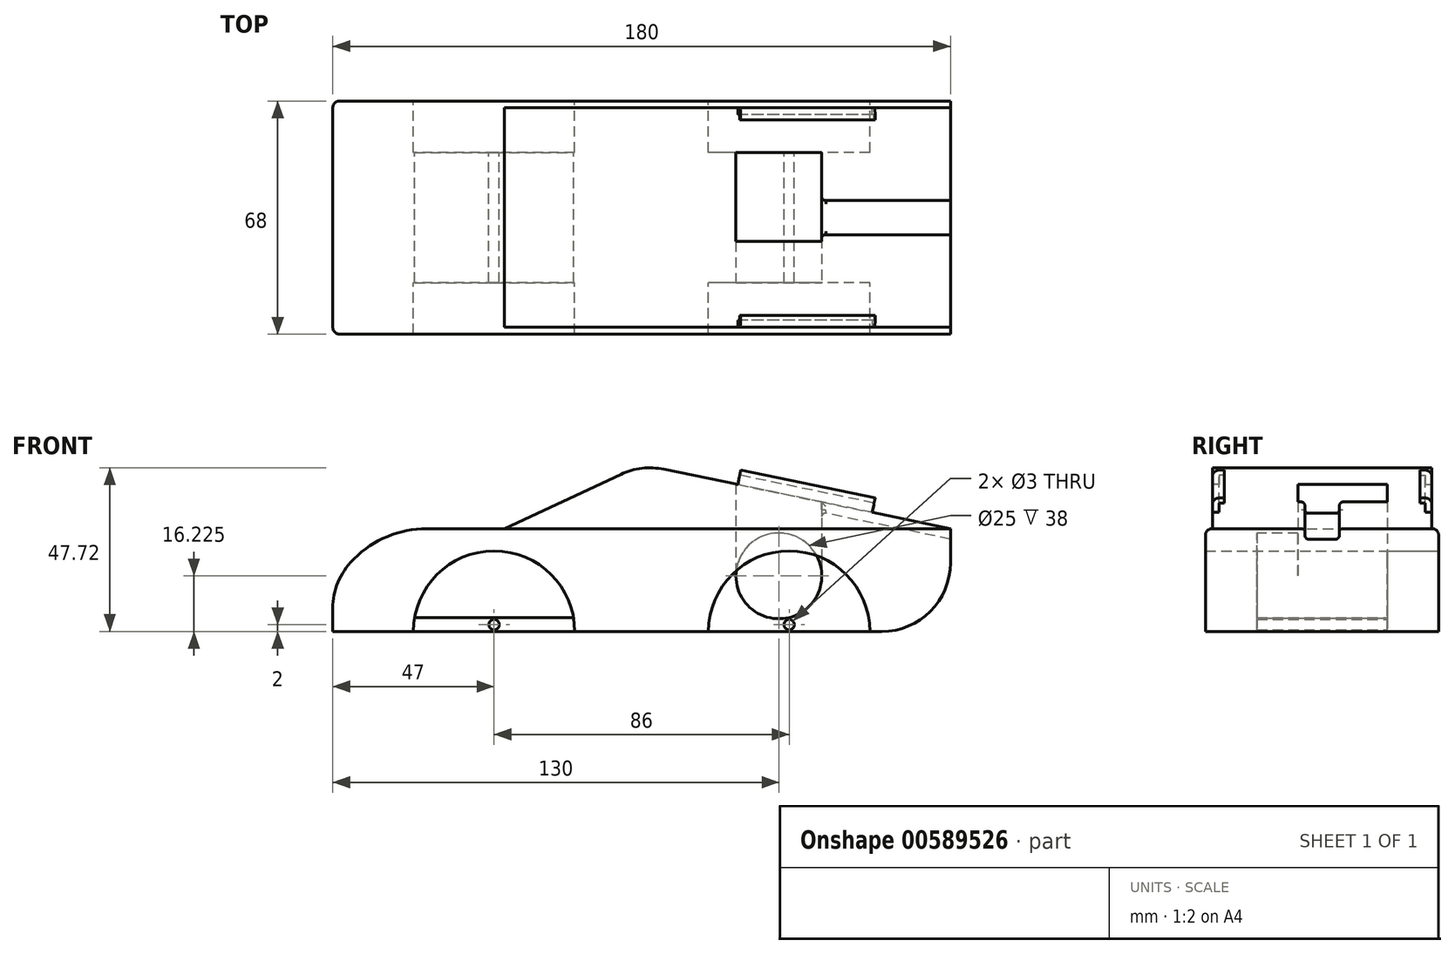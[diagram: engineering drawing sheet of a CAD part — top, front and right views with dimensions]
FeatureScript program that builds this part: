
annotation { "Feature Type Name" : "Feature", "Feature Type Description" : "" }
export const myFeature = defineFeature(function(context is Context, id is Id, definition is map)
    precondition{}
    {
        {
            var Q0;
            Q0=qCreatedBy(makeId("Front.planeOp"),FACE);
            var sketch = newSketch(context, id + "F0", { "sketchPlane" : qUnion([Q0])});
            skLineSegment(sketch, "E0.bottom", {"start": v(90, 15) * mm, "end": v(-75, 15) * mm});
            skLineSegment(sketch, "E0.top", {"start": v(90, -15) * mm, "end": v(-90, -15) * mm});
            skLineSegment(sketch, "E0.left", {"start": v(90, 15) * mm, "end": v(90, -15) * mm});
            skLineSegment(sketch, "E0.right", {"start": v(-90, 0) * mm, "end": v(-90, -15) * mm});
            skPoint(sketch, "E0.middle", {"position": v(0, 0) * mm});
            skLineSegment(sketch, "E1", {"start": v(-90, 0) * mm, "end": v(-75, 15) * mm});
            skLineSegment(sketch, "E2", {"start": v(0, 33.65) * mm, "end": v(-40, 15) * mm});
            skLineSegment(sketch, "E3", {"start": v(0, 33.65) * mm, "end": v(90, 15) * mm});
            skPoint(sketch, "E4.orphan", {"position": v(-90, 15) * mm});
            skCircle(sketch, "E5", {"center": v(40, 1.22) * mm, "radius": 12.5 * mm});
            skArc(sketch, "E6", {"start": v(66.5, -15) * mm, "mid": v(43, 8.5) * mm, "end": v(19.5, -15) * mm});
            skArc(sketch, "E7", {"start": v(-19.5, -15) * mm, "mid": v(-43, 8.5) * mm, "end": v(-66.5, -15) * mm});
            skCircle(sketch, "E8", {"center": v(43, -13) * mm, "radius": 1.5 * mm});
            skCircle(sketch, "E9", {"center": v(-43, -13) * mm, "radius": 1.5 * mm});
            skLineSegment(sketch, "E10", {"start": v(-66.16, -11) * mm, "end": v(-19.84, -11) * mm});
            skSolve(sketch);
        }
        {
            var Q0;
            {var subQ7=sQuery(id+"F0.wireOp",EDGE,"E0.left");Q0=makeQuery(id+"F0.imprint","IMPRINT",FACE,{"disambiguationData":[TD([[makeQuery(id+"F0.imprint","IMPRINT",EDGE,{"derivedFrom":subQ7}),-1.0]])]});}
            var Q1;
            {var subQ0=sQuery(id+"F0.wireOp",EDGE,"E6");var subQ1=sQuery(id+"F0.wireOp",EDGE,"E5");var subQ2=makeQuery(id+"F0.imprint","INTERSECT",VERTEX,{"disambiguationData":[OD(0.0)],"derivedFrom":[subQ1,subQ0]});Q1=makeQuery(id+"F0.imprint","IMPRINT",FACE,{"disambiguationData":[TD([[makeQuery(id+"F0.imprint","IMPRINT",EDGE,{"disambiguationData":[TD([[subQ2,-1.0]])],"derivedFrom":subQ1}),1.0]])]});}
            extrude(context, id + "F1", {"entities" : qUnion([Q0, Q1]), "endBound" : BoundingType.SYMMETRIC, "depth" : 68 * mm, "offsetDistance" : 25 * mm});
        }
        {
            var Q0;
            {var subQ2=sQuery(id+"F0.wireOp",EDGE,"E2");Q0=makeQuery(id+"F0.imprint","IMPRINT",FACE,{"disambiguationData":[TD([[makeQuery(id+"F0.imprint","IMPRINT",EDGE,{"derivedFrom":subQ2}),1.0]])]});}
            extrude(context, id + "F2", {"entities" : qUnion([Q0]), "operationType" : NewBodyOperationType.ADD, "endBound" : BoundingType.SYMMETRIC, "depth" : 64 * mm, "offsetDistance" : 25 * mm});
        }
        {
            var Q0;
            {var subQ0=sQuery(id+"F0.wireOp",EDGE,"E7");Q0=makeQuery(id+"F0.imprint","IMPRINT",FACE,{"disambiguationData":[TD([[makeQuery(id+"F0.imprint","IMPRINT",EDGE,{"derivedFrom":subQ0}),1.0]])]});}
            var Q1;
            {var subQ0=sQuery(id+"F0.wireOp",EDGE,"E6");var subQ1=sQuery(id+"F0.wireOp",EDGE,"E0.top");var subQ2=makeQuery(id+"F0.imprint","INTERSECT",VERTEX,{"disambiguationData":[OD(0.0)],"derivedFrom":[subQ1,subQ0]});Q1=makeQuery(id+"F0.imprint","IMPRINT",FACE,{"disambiguationData":[TD([[makeQuery(id+"F0.imprint","IMPRINT",EDGE,{"disambiguationData":[TD([[subQ2,-1.0]])],"derivedFrom":subQ1}),-1.0]])]});}
            var Q2;
            {var subQ0=sQuery(id+"F0.wireOp",EDGE,"E6");var subQ1=sQuery(id+"F0.wireOp",EDGE,"E5");var subQ2=makeQuery(id+"F0.imprint","INTERSECT",VERTEX,{"disambiguationData":[OD(0.0)],"derivedFrom":[subQ1,subQ0]});Q2=makeQuery(id+"F0.imprint","IMPRINT",FACE,{"disambiguationData":[TD([[makeQuery(id+"F0.imprint","IMPRINT",EDGE,{"disambiguationData":[TD([[subQ2,1.0]])],"derivedFrom":subQ1}),1.0]])]});}
            extrude(context, id + "F3", {"entities" : qUnion([Q0, Q1, Q2]), "operationType" : NewBodyOperationType.ADD, "endBound" : BoundingType.SYMMETRIC, "depth" : 38 * mm, "offsetDistance" : 25 * mm});
        }
        {
            var Q0;
            Q0=makeQuery(id+"F3.opExtrude","CAP_FACE",FACE,{"disambiguationData":[OSD([sQuery(id+"F0.wireOp",EDGE,"E0.top"),sQuery(id+"F0.wireOp",EDGE,"E6")])],"isStart":false});
            var sketch = newSketch(context, id + "F4", { "sketchPlane" : qUnion([Q0])});
            skCircle(sketch, "E11.0", {"center": v(40, 1.22) * mm, "radius": 12.5 * mm});
            skSolve(sketch);
        }
        {
            var Q0;
            Q0 = qSketchRegion(id + "F4", true);
            extrude(context, id + "F5", {"entities" : qUnion([Q0]), "operationType" : NewBodyOperationType.REMOVE, "oppositeDirection" : true, "depth" : 38 * mm, "offsetDistance" : 25 * mm});
        }
        {
            var Q0;
            Q0=qCreatedBy(makeId("Top.planeOp"),FACE);
            cPlane(context, id + "F6", {"entities" : qUnion([Q0]), "cplaneType" : CPlaneType.OFFSET, "offset" : 1.23 * mm, "width" : 150 * mm, "height" : 150 * mm});
        }
        {
            var Q0;
            Q0=qCreatedBy(id+"F6.planeOp",FACE);
            var sketch = newSketch(context, id + "F7", { "sketchPlane" : qUnion([Q0])});
            skLineSegment(sketch, "E12", {"start": v(27.5, 19) * mm, "end": v(27.5, -7) * mm});
            skLineSegment(sketch, "E13", {"start": v(27.5, -7) * mm, "end": v(52.5, -7) * mm});
            skLineSegment(sketch, "E14", {"start": v(52.5, -7) * mm, "end": v(52.5, 19) * mm});
            skLineSegment(sketch, "E15", {"start": v(52.5, 19) * mm, "end": v(27.5, 19) * mm});
            skSolve(sketch);
        }
        {
            var Q0;
            Q0 = qSketchRegion(id + "F7", true);
            extrude(context, id + "F8", {"entities" : qUnion([Q0]), "operationType" : NewBodyOperationType.REMOVE, "endBound" : BoundingType.THROUGH_ALL, "depth" : 25 * mm, "offsetDistance" : 25 * mm});
        }
        {
            var Q0;
            Q0=makeQuery(id+"F2.opExtrude","SWEPT_EDGE",EDGE,{"disambiguationData":[OSD([sQuery(id+"F0.wireOp",EDGE,"E2"),sQuery(id+"F0.wireOp",EDGE,"E3")])]});
            var Q1;
            Q1=makeQuery(id+"F1.opExtrude","SWEPT_EDGE",EDGE,{"disambiguationData":[OSD([sQuery(id+"F0.wireOp",EDGE,"E0.right"),sQuery(id+"F0.wireOp",EDGE,"E1")])]});
            fillet(context, id + "F9", {"entities" : qUnion([Q0, Q1]), "radius" : 20 * mm, "tangentPropagation" : true, "allowEdgeOverflow" : false});
        }
        {
            var Q0;
            Q0=makeQuery(id+"F1.opExtrude","SWEPT_EDGE",EDGE,{"disambiguationData":[OSD([sQuery(id+"F0.wireOp",EDGE,"E0.bottom"),sQuery(id+"F0.wireOp",EDGE,"E1")])]});
            fillet(context, id + "F10", {"entities" : qUnion([Q0]), "radius" : 30 * mm, "tangentPropagation" : true, "allowEdgeOverflow" : false});
        }
        {
            var Q0;
            Q0=makeQuery(id+"F1.opExtrude","CAP_EDGE",EDGE,{"disambiguationData":[OSD([sQuery(id+"F0.wireOp",EDGE,"E0.bottom")])],"isStart":false});
            var Q1;
            Q1=makeQuery(id+"F1.opExtrude","CAP_EDGE",EDGE,{"disambiguationData":[OSD([sQuery(id+"F0.wireOp",EDGE,"E0.bottom")])],"isStart":true});
            fillet(context, id + "F11", {"entities" : qUnion([Q0, Q1]), "radius" : 2 * mm, "tangentPropagation" : true, "allowEdgeOverflow" : false});
        }
        {
            var Q0;
            Q0=makeQuery(id+"F1.opExtrude","SWEPT_EDGE",EDGE,{"disambiguationData":[OSD([sQuery(id+"F0.wireOp",EDGE,"E0.top"),sQuery(id+"F0.wireOp",EDGE,"E0.left")])]});
            fillet(context, id + "F12", {"entities" : qUnion([Q0]), "radius" : 20 * mm, "tangentPropagation" : true, "allowEdgeOverflow" : false});
        }
        {
            var Q0;
            Q0=makeQuery(id+"F2.opExtrude","SWEPT_FACE",FACE,{"disambiguationData":[OSD([sQuery(id+"F0.wireOp",EDGE,"E3")])]});
            var Q1;
            Q1=makeQuery(id+"F8.boolean.opBoolean","INTERSECT",EDGE,{"derivedFrom":[makeQuery(id+"F2.opExtrude","SWEPT_FACE",FACE,{"disambiguationData":[OSD([sQuery(id+"F0.wireOp",EDGE,"E3")])]}),makeQuery(id+"F8.opExtrude","SWEPT_FACE",FACE,{"disambiguationData":[OSD([sQuery(id+"F7.wireOp",EDGE,"E14")])]})]});
            cPlane(context, id + "F13", {"entities" : qUnion([Q0, Q1]), "cplaneType" : CPlaneType.LINE_ANGLE, "offset" : 25 * mm, "angle" : 90 * degree, "width" : 150 * mm, "height" : 150 * mm});
        }
        {
            var Q0;
            Q0=qCreatedBy(id+"F13.planeOp",FACE);
            var sketch = newSketch(context, id + "F14", { "sketchPlane" : qUnion([Q0])});
            skPoint(sketch, "E16.0", {"position": v(-32, 32.95) * mm});
            skPoint(sketch, "E16.1", {"position": v(32, 32.95) * mm});
            skLineSegment(sketch, "E17", {"start": v(0, 32.95) * mm, "end": v(0, 48.45) * mm, "construction": true});
            skLineSegment(sketch, "E18", {"start": v(-32, 32.95) * mm, "end": v(-32, 37.25) * mm});
            skLineSegment(sketch, "E19", {"start": v(-32, 37.25) * mm, "end": v(-28.5, 37.25) * mm});
            skLineSegment(sketch, "E20", {"start": v(-28.5, 37.25) * mm, "end": v(-28.5, 35.75) * mm});
            skLineSegment(sketch, "E21", {"start": v(-28.5, 35.75) * mm, "end": v(-30, 35.75) * mm});
            skLineSegment(sketch, "E22", {"start": v(-30, 35.75) * mm, "end": v(-30, 32.95) * mm});
            skLineSegment(sketch, "E23", {"start": v(-30, 32.95) * mm, "end": v(-32, 32.95) * mm});
            skLineSegment(sketch, "E24.MirrorCS", {"start": v(30, 35.75) * mm, "end": v(30, 32.95) * mm});
            skLineSegment(sketch, "E25.MirrorCS", {"start": v(32, 32.95) * mm, "end": v(32, 37.25) * mm});
            skLineSegment(sketch, "E26.MirrorCS", {"start": v(28.5, 35.75) * mm, "end": v(30, 35.75) * mm});
            skLineSegment(sketch, "E27.MirrorCS", {"start": v(30, 32.95) * mm, "end": v(32, 32.95) * mm});
            skLineSegment(sketch, "E28.MirrorCS", {"start": v(28.5, 37.25) * mm, "end": v(28.5, 35.75) * mm});
            skLineSegment(sketch, "E29.MirrorCS", {"start": v(32, 37.25) * mm, "end": v(28.5, 37.25) * mm});
            skSolve(sketch);
        }
        {
            var Q0;
            Q0=makeQuery(id+"F14.imprint","IMPRINT",FACE,{"disambiguationData":[TD([[makeQuery(id+"F14.imprint","IMPRINT",EDGE,{"derivedFrom":sQuery(id+"F14.wireOp",EDGE,"E18")}),-1.0]])]});
            var Q1;
            Q1=makeQuery(id+"F14.imprint","IMPRINT",FACE,{"disambiguationData":[TD([[makeQuery(id+"F14.imprint","IMPRINT",EDGE,{"derivedFrom":sQuery(id+"F14.wireOp",EDGE,"E24.MirrorCS")}),1.0]])]});
            extrude(context, id + "F15", {"entities" : qUnion([Q0, Q1]), "operationType" : NewBodyOperationType.ADD, "depth" : 15 * mm, "offsetDistance" : 25 * mm, "hasSecondDirection" : true, "secondDirectionOppositeDirection" : true, "secondDirectionDepth" : 25 * mm});
        }
        {
            var Q0;
            Q0=makeQuery(id+"F15.opExtrude","SWEPT_EDGE",EDGE,{"disambiguationData":[OSD([sQuery(id+"F14.wireOp",EDGE,"E18"),sQuery(id+"F14.wireOp",EDGE,"E19")])]});
            var Q1;
            Q1=makeQuery(id+"F15.opExtrude","SWEPT_EDGE",EDGE,{"disambiguationData":[OSD([sQuery(id+"F14.wireOp",EDGE,"E25.MirrorCS"),sQuery(id+"F14.wireOp",EDGE,"E29.MirrorCS")])]});
            fillet(context, id + "F16", {"entities" : qUnion([Q0, Q1]), "radius" : 2 * mm, "tangentPropagation" : true, "allowEdgeOverflow" : false});
        }
        {
            var Q0;
            Q0=qCreatedBy(id+"F13.planeOp",FACE);
            var sketch = newSketch(context, id + "F17", { "sketchPlane" : qUnion([Q0])});
            skPoint(sketch, "E30.0", {"position": v(0, 32.95) * mm});
            skLineSegment(sketch, "E31.bottom", {"start": v(5, 29.95) * mm, "end": v(-5, 29.95) * mm});
            skLineSegment(sketch, "E31.top", {"start": v(5, 35.95) * mm, "end": v(-5, 35.95) * mm});
            skLineSegment(sketch, "E31.left", {"start": v(5, 29.95) * mm, "end": v(5, 35.95) * mm});
            skLineSegment(sketch, "E31.right", {"start": v(-5, 29.95) * mm, "end": v(-5, 35.95) * mm});
            skSolve(sketch);
        }
        {
            var Q0;
            Q0=makeQuery(id+"F17.imprint","IMPRINT",FACE,{"disambiguationData":[TD([[makeQuery(id+"F17.imprint","IMPRINT",EDGE,{"derivedFrom":sQuery(id+"F17.wireOp",EDGE,"E31.bottom")}),-1.0]])]});
            extrude(context, id + "F18", {"entities" : qUnion([Q0]), "operationType" : NewBodyOperationType.REMOVE, "depth" : 40 * mm, "offsetDistance" : 25 * mm});
        }
        {
            var Q0;
            Q0=makeQuery(id+"F18.boolean.opBoolean","INTERSECT",EDGE,{"derivedFrom":[makeQuery(id+"F8.boolean.opBoolean","COPY",FACE,{"derivedFrom":makeQuery(id+"F8.opExtrude","SWEPT_FACE",FACE,{"disambiguationData":[OSD([sQuery(id+"F7.wireOp",EDGE,"E14")])]})}),makeQuery(id+"F18.opExtrude","SWEPT_FACE",FACE,{"disambiguationData":[OSD([sQuery(id+"F17.wireOp",EDGE,"E31.bottom")])]})]});
            var Q1;
            Q1=makeQuery(id+"F18.boolean.opBoolean","INTERSECT",EDGE,{"derivedFrom":[makeQuery(id+"F8.boolean.opBoolean","COPY",FACE,{"derivedFrom":makeQuery(id+"F8.opExtrude","SWEPT_FACE",FACE,{"disambiguationData":[OSD([sQuery(id+"F7.wireOp",EDGE,"E14")])]})}),makeQuery(id+"F18.opExtrude","SWEPT_FACE",FACE,{"disambiguationData":[OSD([sQuery(id+"F17.wireOp",EDGE,"E31.right")])]})]});
            var Q2;
            Q2=makeQuery(id+"F18.boolean.opBoolean","INTERSECT",EDGE,{"derivedFrom":[makeQuery(id+"F8.boolean.opBoolean","COPY",FACE,{"derivedFrom":makeQuery(id+"F8.opExtrude","SWEPT_FACE",FACE,{"disambiguationData":[OSD([sQuery(id+"F7.wireOp",EDGE,"E14")])]})}),makeQuery(id+"F18.opExtrude","SWEPT_FACE",FACE,{"disambiguationData":[OSD([sQuery(id+"F17.wireOp",EDGE,"E31.left")])]})]});
            var Q3;
            Q3=makeQuery(id+"F18.boolean.opBoolean","COPY",EDGE,{"derivedFrom":makeQuery(id+"F18.opExtrude","SWEPT_EDGE",EDGE,{"disambiguationData":[OSD([sQuery(id+"F17.wireOp",EDGE,"E31.bottom"),sQuery(id+"F17.wireOp",EDGE,"E31.right")])]})});
            var Q4;
            Q4=makeQuery(id+"F18.boolean.opBoolean","COPY",EDGE,{"derivedFrom":makeQuery(id+"F18.opExtrude","SWEPT_EDGE",EDGE,{"disambiguationData":[OSD([sQuery(id+"F17.wireOp",EDGE,"E31.bottom"),sQuery(id+"F17.wireOp",EDGE,"E31.left")])]})});
            var Q5;
            Q5=makeQuery(id+"F18.boolean.opBoolean","INTERSECT",EDGE,{"derivedFrom":[makeQuery(id+"F2.opExtrude","SWEPT_FACE",FACE,{"disambiguationData":[OSD([sQuery(id+"F0.wireOp",EDGE,"E3")])]}),makeQuery(id+"F18.opExtrude","SWEPT_FACE",FACE,{"disambiguationData":[OSD([sQuery(id+"F17.wireOp",EDGE,"E31.right")])]})]});
            var Q6;
            Q6=makeQuery(id+"F18.boolean.opBoolean","INTERSECT",EDGE,{"derivedFrom":[makeQuery(id+"F2.opExtrude","SWEPT_FACE",FACE,{"disambiguationData":[OSD([sQuery(id+"F0.wireOp",EDGE,"E3")])]}),makeQuery(id+"F18.opExtrude","SWEPT_FACE",FACE,{"disambiguationData":[OSD([sQuery(id+"F17.wireOp",EDGE,"E31.left")])]})]});
            fillet(context, id + "F19", {"entities" : qUnion([Q0, Q1, Q2, Q3, Q4, Q5, Q6]), "radius" : 1 * mm, "tangentPropagation" : true, "allowEdgeOverflow" : false});
        }
    });
